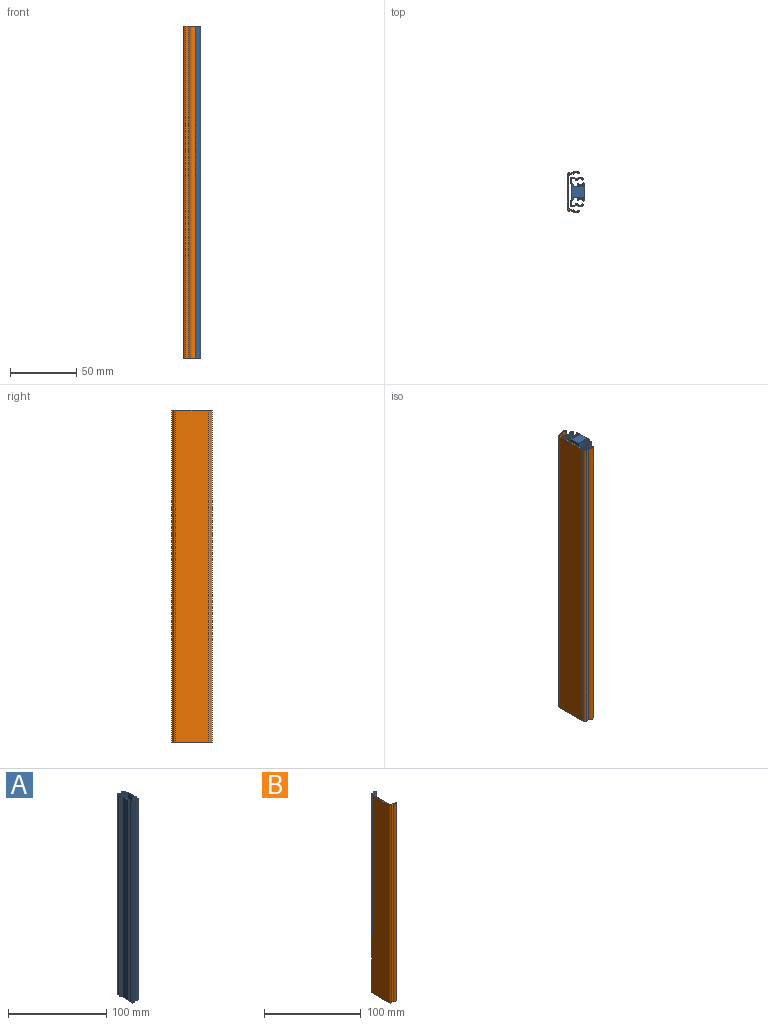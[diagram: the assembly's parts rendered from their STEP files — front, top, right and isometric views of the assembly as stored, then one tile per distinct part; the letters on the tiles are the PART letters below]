
ASSEMBLY  parts=2 mates=1
PART A: 66 faces, bbox 10.6x22.1x250 mm
  f0: plane 250x9.94mm, normal (1,0,0), area 2445.7mm2, adj f13,f14,f48,f49,f63,f64,f65
  f1: cylinder r=2.96mm len=250mm, axis (0,0,-1), area 1490.1mm2, adj f2,f47,f48,f49
  f2: plane 250x0.57mm, normal (0.7,0.72,0), area 198.7mm2, adj f1,f3,f48,f49
  f3: cylinder r=2.7mm len=250mm, axis (0,0,-1), area 1344.8mm2, adj f2,f4,f48,f49
  f4: plane 250x0.5mm, normal (0,1,0), area 124.7mm2, adj f3,f5,f48,f49
  f5: cylinder r=0.66mm len=250mm, axis (0,0,-1), area 104.6mm2, adj f4,f6,f48,f49
  f6: plane 250x1.18mm, normal (-0.65,0.76,0), area 387.5mm2, adj f5,f7,f48,f49
  f7: cylinder r=0.61mm len=250mm, axis (0,0,-1), area 95.5mm2, adj f6,f8,f48,f49
  f8: plane 250x0.73mm, normal (0,1,0), area 182.4mm2, adj f7,f9,f48,f49
  f9: cylinder r=0.71mm len=250mm, axis (0,0,-1), area 284.5mm2, adj f8,f10,f48,f49
  f10: plane 250x2.14mm, normal (1,0,0), area 535.7mm2, adj f9,f11,f48,f49
  f11: cylinder r=0.7mm len=250mm, axis (0,0,-1), area 133.5mm2, adj f10,f12,f48,f49
  f12: plane 250x1.55mm, normal (0.84,-0.54,0), area 458.5mm2, adj f11,f13,f48,f49
  f13: cylinder r=0.61mm len=250mm, axis (0,0,-1), area 86.8mm2, adj f0,f12,f48,f49
  f14: cylinder r=0.61mm len=250mm, axis (0,0,-1), area 86.8mm2, adj f0,f15,f48,f49
  f15: plane 250x1.55mm, normal (0.84,0.54,0), area 458.5mm2, adj f14,f16,f48,f49
  f16: cylinder r=0.7mm len=250mm, axis (0,0,-1), area 133.5mm2, adj f15,f17,f48,f49
  f17: plane 250x2.14mm, normal (1,0,0), area 535.7mm2, adj f16,f18,f48,f49
  f18: cylinder r=0.71mm len=250mm, axis (0,0,-1), area 284.5mm2, adj f17,f19,f48,f49
  f19: plane 250x0.73mm, normal (0,-1,0), area 182.4mm2, adj f18,f20,f48,f49
  f20: cylinder r=0.61mm len=250mm, axis (0,0,-1), area 95.5mm2, adj f19,f21,f48,f49
  f21: plane 250x1.18mm, normal (-0.65,-0.76,0), area 387.5mm2, adj f20,f22,f48,f49
  f22: cylinder r=0.66mm len=250mm, axis (0,0,-1), area 104.6mm2, adj f21,f23,f48,f49
  f23: plane 250x0.5mm, normal (0,-1,0), area 124.7mm2, adj f22,f24,f48,f49
  f24: cylinder r=2.7mm len=250mm, axis (0,0,-1), area 1344.8mm2, adj f23,f25,f48,f49
  f25: plane 250x0.57mm, normal (0.7,-0.72,0), area 198.7mm2, adj f24,f26,f48,f49
  f26: cylinder r=2.96mm len=250mm, axis (0,0,-1), area 1490.1mm2, adj f25,f27,f48,f49
  f27: plane 250x0.46mm, normal (0,1,0), area 115.5mm2, adj f26,f28,f48,f49
  f28: cylinder r=0.59mm len=250mm, axis (0,0,-1), area 115.8mm2, adj f27,f29,f48,f49
  f29: plane 250x1.26mm, normal (0.64,0.77,0), area 409.2mm2, adj f28,f30,f48,f49
  f30: cylinder r=0.95mm len=250mm, axis (0,0,-1), area 124.7mm2, adj f29,f31,f48,f49
  f31: plane 250x1.03mm, normal (0,1,0), area 258.5mm2, adj f30,f32,f48,f49
  f32: cylinder r=1.26mm len=250mm, axis (0,0,-1), area 517.9mm2, adj f31,f33,f48,f49
  f33: plane 250x2.35mm, normal (-1,0,0), area 587.2mm2, adj f32,f34,f48,f49
  f34: cylinder r=1.18mm len=250mm, axis (0,0,-1), area 221.8mm2, adj f33,f35,f48,f49
  f35: plane 250x1.2mm, normal (-0.87,-0.49,0), area 344.8mm2, adj f34,f36,f48,f49
  f36: cylinder r=0.72mm len=250mm, axis (0,0,-1), area 111mm2, adj f35,f37,f48,f49
  f37: plane 250x9.81mm, normal (-1,0,0), area 2451.6mm2, adj f36,f38,f48,f49
  f38: cylinder r=0.72mm len=250mm, axis (0,0,-1), area 111mm2, adj f37,f39,f48,f49
  f39: plane 250x1.2mm, normal (-0.87,0.49,0), area 344.8mm2, adj f38,f40,f48,f49
  f40: cylinder r=1.18mm len=250mm, axis (0,0,-1), area 221.8mm2, adj f39,f41,f48,f49
  f41: plane 250x2.35mm, normal (-1,0,0), area 587.2mm2, adj f40,f42,f48,f49
  f42: cylinder r=1.26mm len=250mm, axis (0,0,-1), area 517.9mm2, adj f41,f43,f48,f49
  f43: plane 250x1.03mm, normal (0,-1,0), area 258.5mm2, adj f42,f44,f48,f49
  f44: cylinder r=0.95mm len=250mm, axis (0,0,-1), area 124.7mm2, adj f43,f45,f48,f49
  f45: plane 250x1.26mm, normal (0.64,-0.77,0), area 409.2mm2, adj f44,f46,f48,f49
  f46: cylinder r=0.59mm len=250mm, axis (0,0,-1), area 115.8mm2, adj f45,f47,f48,f49
  f47: plane 250x0.46mm, normal (0,-1,0), area 115.5mm2, adj f1,f46,f48,f49
  f48: plane 22.12x9.9mm, normal (0,0,1), area 37.2mm2, adj f0,f1,f2,f3,f4,f5,f6,f7
  f49: plane 22.12x10.61mm, normal (0,0,-1), area 114.4mm2, adj f0,f1,f2,f3,f4,f5,f6,f7
  f50: plane 250x9.91mm, normal (-1,0,0), area 2438.2mm2, adj f49,f60,f61,f62,f63,f64,f65
  f51: cylinder r=3.4mm len=250mm, axis (0,0,-1), area 1252.4mm2, adj f49,f52,f61,f62
  f52: plane 250x0.53mm, normal (-0.68,-0.73,0), area 181.7mm2, adj f49,f51,f53,f62
  f53: cylinder r=2.81mm len=250mm, axis (0,0,-1), area 1206mm2, adj f49,f52,f54,f62
  f54: cylinder r=1.73mm len=250mm, axis (0,0,-1), area 488.4mm2, adj f49,f53,f55,f62
  f55: plane 250x10.38mm, normal (1,0,0), area 2595.4mm2, adj f49,f54,f56,f62
  f56: cylinder r=1.73mm len=250mm, axis (0,0,-1), area 488.4mm2, adj f49,f55,f57,f62
  f57: cylinder r=2.81mm len=250mm, axis (0,0,-1), area 1206mm2, adj f49,f56,f58,f62
  f58: plane 250x0.53mm, normal (-0.68,0.73,0), area 181.7mm2, adj f49,f57,f59,f62
  f59: cylinder r=3.4mm len=250mm, axis (0,0,-1), area 1252.4mm2, adj f49,f58,f60,f62
  f60: cylinder r=0.53mm len=250mm, axis (0,0,-1), area 180.8mm2, adj f49,f50,f59,f62
  f61: cylinder r=0.53mm len=250mm, axis (0,0,-1), area 180.8mm2, adj f49,f50,f51,f62
  f62: plane 13.53x5.71mm, normal (0,0,1), area 18mm2, adj f50,f51,f52,f53,f54,f55,f56,f57
  f63: plane 7.72x7.67mm, normal (0,0,1), area 59.2mm2, adj f0,f50,f64,f65
  f64: plane 7.67x5mm, normal (0,1,0), area 38.3mm2, adj f0,f49,f50,f63
  f65: plane 7.67x5mm, normal (0,-1,0), area 38.3mm2, adj f0,f49,f50,f63
PART B: 18 faces, bbox 8.9x30.9x250 mm
  f0: plane 250x0.62mm, normal (0.65,0.76,0), area 205.4mm2, adj f1,f15,f16,f17
  f1: cylinder r=2.25mm len=250mm, axis (0,0,-1), area 1182.1mm2, adj f0,f2,f16,f17
  f2: plane 250x2.13mm, normal (0,1,0), area 531.7mm2, adj f1,f3,f16,f17
  f3: cylinder r=1.09mm len=250mm, axis (0,0,-1), area 432.9mm2, adj f2,f4,f16,f17
  f4: plane 250x24.51mm, normal (1,0,0), area 6126.4mm2, adj f3,f5,f16,f17
  f5: cylinder r=1.09mm len=250mm, axis (0,0,-1), area 432.9mm2, adj f4,f6,f16,f17
  f6: plane 250x2.13mm, normal (0,-1,0), area 531.7mm2, adj f5,f7,f16,f17
  f7: cylinder r=2.25mm len=250mm, axis (0,0,-1), area 1182.1mm2, adj f6,f8,f16,f17
  f8: plane 250x0.62mm, normal (0.65,-0.76,0), area 205.4mm2, adj f7,f9,f16,f17
  f9: cylinder r=3.11mm len=250mm, axis (0,0,-1), area 1381.1mm2, adj f8,f10,f16,f17
  f10: plane 250x2.25mm, normal (0,1,0), area 562mm2, adj f9,f11,f16,f17
  f11: cylinder r=1.8mm len=250mm, axis (0,0,-1), area 715mm2, adj f10,f12,f16,f17
  f12: plane 250x24.82mm, normal (-1,0,0), area 6204.2mm2, adj f11,f13,f16,f17
  f13: cylinder r=1.8mm len=250mm, axis (0,0,-1), area 715mm2, adj f12,f14,f16,f17
  f14: plane 250x2.25mm, normal (0,-1,0), area 562mm2, adj f13,f15,f16,f17
  f15: cylinder r=3.11mm len=250mm, axis (0,0,-1), area 1381.1mm2, adj f0,f14,f16,f17
  f16: plane 30.87x8.85mm, normal (0,0,1), area 45.2mm2, adj f0,f1,f2,f3,f4,f5,f6,f7
  f17: plane 30.87x8.85mm, normal (0,0,-1), area 45.2mm2, adj f0,f1,f2,f3,f4,f5,f6,f7
PLACE A rot(axis=(1,0,0),180deg) t=(-68.22,-83.39,202.25)mm
PLACE B t=(-68.83,-53.99,-47.75)mm
MATE slider A.f48 <-> B.f16  axis (0,0,-1) through (-212.58,-68.69,-47.75)mm
